# Revit family: Toilet-Floor_Mount_Hidden_Cord-KOHLER-San_Raphael-K-3722T_1
name_source: partatom
category: Plumbing Fixtures
units: mm (PartAtom-declared; Revit-internal decimal feet)

## family parameters
Cut with Voids When Loaded = No
Host = Face
OmniClass Number = 23.31.19.00
OmniClass Title = Toilets
Part Type = Normal
Room Calculation Point = No
Round Connector Dimension = Use Diameter
Shared = No

## types (1)
- 0-White
    ADA Compliant = No
    Apparent Load = 2200 VA
    Assembly Code = D2010100
    CW Connection = Yes
    Cold Water Inlet = Cold Water Inlet
    Date Modified = 08/31/2023
    Default Elevation = 0"
    Description = 1 PIECE TOILET HIDDEN CORD 305MM WITHOUT TOILET SEAT
    Electrical Connector = Yes
    Electrical Note = Ground-Fault Circuit-Interrupter
    Finish = Kohler-Vitreous_China-0-White
    Flow Rate = 0 GPM
    Flush Rate- GPF = 0 GPF
    Flush Rate- LPF = 0 LPF
    HW Connection = No
    Handle Material = Kohler-Metal-CP-Polished_Chrome
    Height = 24"
    Hot Water Inlet = Hot Water Inlet
    Length = 28 7/16"
    Manufacturer = Kohler Co.
    MasterFormat 2014 = 22 42 13.13
    MasterFormat 2014 Name = Residential Water Closets
    Material = Vitreous China
    Model = K-3722T-HC-0
    Pressure = 0.00 psi
    Product Name = SAN RAPHAEL
    Rough-In = 12"
    Seat Cold Water Inlet = Seat Cold Water Inlet
    Seat Included = No
    Type = 1
    URL = http://www.kohler.com.cn
    Vent Connection = No
    Voltage = 220 V
    Waste Connection = Yes
    Waste Water Outlet = Waste Water Outlet
    Width = 20 7/16"

## geometry (parser evidence)
native form markers: Sweep x7
no freeform markers — native parametric forms only
